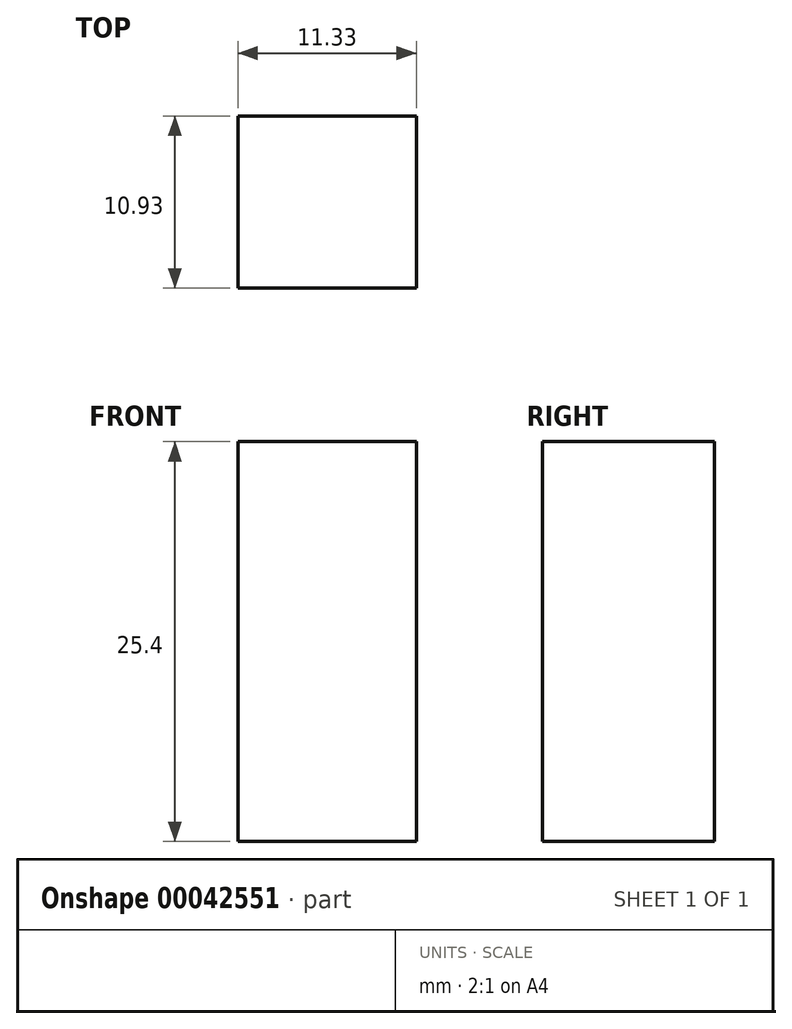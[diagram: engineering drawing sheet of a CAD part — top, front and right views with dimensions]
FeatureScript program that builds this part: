
annotation { "Feature Type Name" : "Feature", "Feature Type Description" : "" }
export const myFeature = defineFeature(function(context is Context, id is Id, definition is map)
    precondition{}
    {
        {
            var Q0;
            Q0=qCreatedBy(makeId("Top.planeOp"),FACE);
            var sketch = newSketch(context, id + "F0", { "sketchPlane" : qUnion([Q0])});
            skLineSegment(sketch, "E0.rect.bottom", {"start": v(-13.96, 8.75) * mm, "end": v(-25.29, 8.75) * mm});
            skLineSegment(sketch, "E0.rect.top", {"start": v(-13.96, 19.68) * mm, "end": v(-25.29, 19.68) * mm});
            skLineSegment(sketch, "E0.rect.left", {"start": v(-13.96, 8.75) * mm, "end": v(-13.96, 19.68) * mm});
            skLineSegment(sketch, "E0.rect.right", {"start": v(-25.29, 8.75) * mm, "end": v(-25.29, 19.68) * mm});
            skPoint(sketch, "E0.rect.middle", {"position": v(-19.63, 14.22) * mm});
            skSolve(sketch);
        }
        {
            var Q0;
            Q0 = qSketchRegion(id + "F0", true);
            extrude(context, id + "F1", {"entities" : qUnion([Q0]), "depth" : 25.4 * mm});
        }
    });
